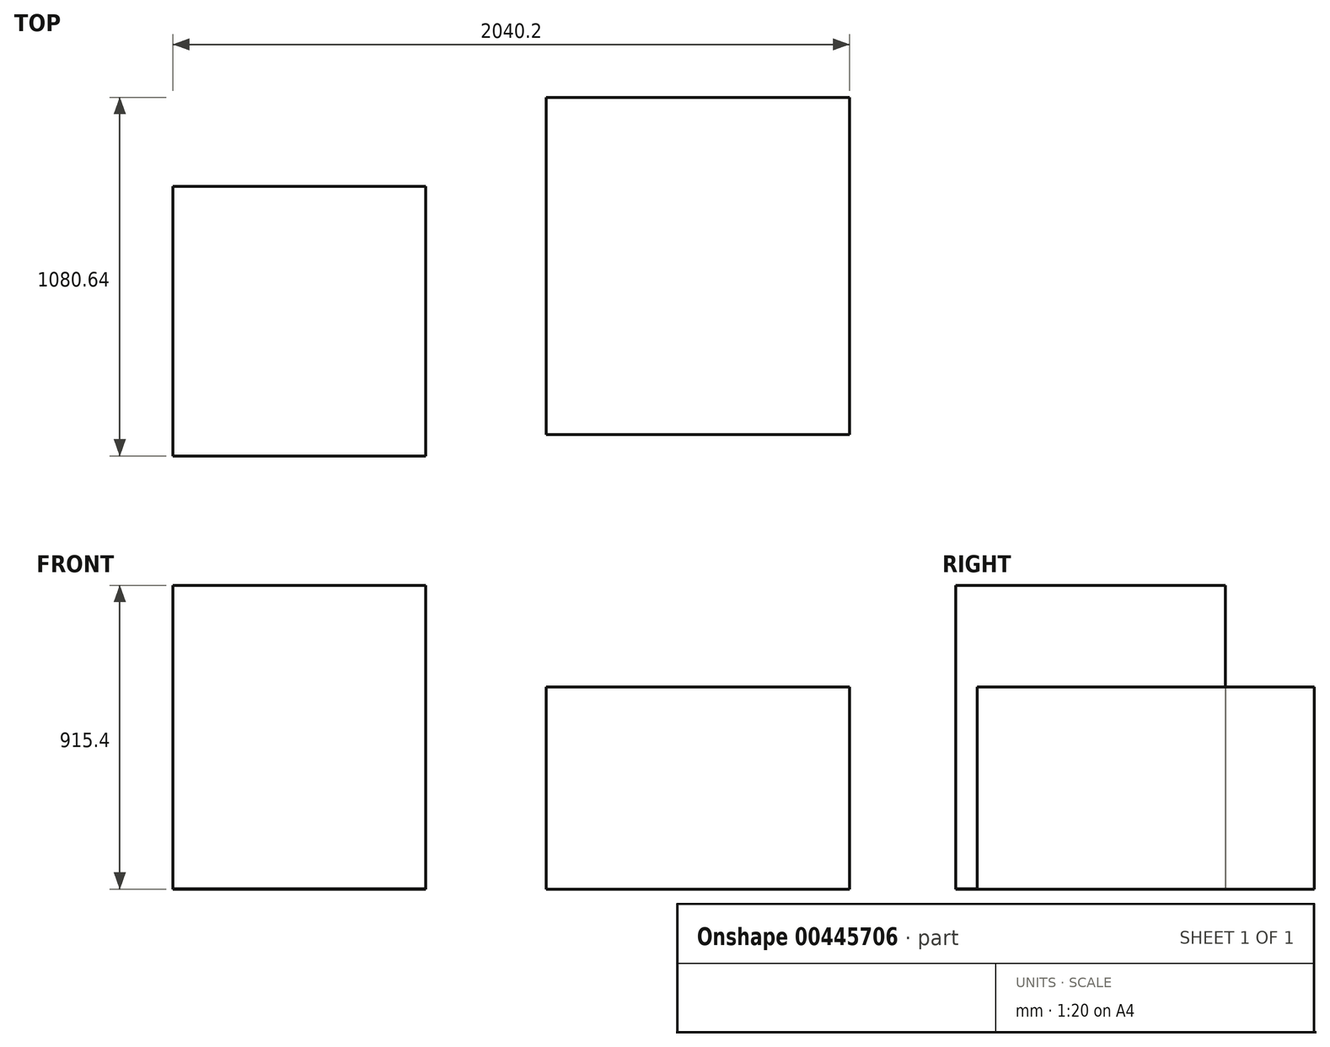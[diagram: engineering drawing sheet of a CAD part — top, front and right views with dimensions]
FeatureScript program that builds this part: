
annotation { "Feature Type Name" : "Feature", "Feature Type Description" : "" }
export const myFeature = defineFeature(function(context is Context, id is Id, definition is map)
    precondition{}
    {
        {
            var Q0;
            Q0=qCreatedBy(makeId("Top.planeOp"),FACE);
            var sketch = newSketch(context, id + "F0", { "sketchPlane" : qUnion([Q0])});
            skLineSegment(sketch, "E0.bottom", {"start": v(-79.69, -64.64) * mm, "end": v(682.31, -64.64) * mm});
            skLineSegment(sketch, "E0.top", {"start": v(-79.69, 748.16) * mm, "end": v(682.31, 748.16) * mm});
            skLineSegment(sketch, "E0.left", {"start": v(-79.69, -64.64) * mm, "end": v(-79.69, 748.16) * mm});
            skLineSegment(sketch, "E0.right", {"start": v(682.31, -64.64) * mm, "end": v(682.31, 748.16) * mm});
            skSolve(sketch);
        }
        {
            var Q0;
            Q0 = qSketchRegion(id + "F0", true);
            extrude(context, id + "F1", {"entities" : qUnion([Q0]), "depth" : 1 * mm});
        }
        {
            var Q0;
            Q0=makeQuery(id+"F1.opExtrude","CAP_FACE",FACE,{"disambiguationData":[OSD([sQuery(id+"F0.wireOp",EDGE,"E0.bottom"),sQuery(id+"F0.wireOp",EDGE,"E0.top"),sQuery(id+"F0.wireOp",EDGE,"E0.left"),sQuery(id+"F0.wireOp",EDGE,"E0.right")])],"isStart":false});
            var sketch = newSketch(context, id + "F2", { "sketchPlane" : qUnion([Q0])});
            skLineSegment(sketch, "E1.bottom", {"start": v(-79.69, -64.64) * mm, "end": v(682.31, -64.64) * mm});
            skLineSegment(sketch, "E1.top", {"start": v(-79.69, 748.16) * mm, "end": v(682.31, 748.16) * mm});
            skLineSegment(sketch, "E1.left", {"start": v(-79.69, -64.64) * mm, "end": v(-79.69, 748.16) * mm});
            skLineSegment(sketch, "E1.right", {"start": v(682.31, -64.64) * mm, "end": v(682.31, 748.16) * mm});
            skSolve(sketch);
        }
        {
            var Q0;
            Q0 = qSketchRegion(id + "F2", true);
            extrude(context, id + "F3", {"entities" : qUnion([Q0]), "depth" : 914.4 * mm});
        }
        {
            var Q0;
            Q0=qCreatedBy(makeId("Top.planeOp"),FACE);
            var sketch = newSketch(context, id + "F4", { "sketchPlane" : qUnion([Q0])});
            skLineSegment(sketch, "E2.bottom", {"start": v(1046.11, 0) * mm, "end": v(1960.51, 0) * mm});
            skLineSegment(sketch, "E2.top", {"start": v(1046.11, 1016) * mm, "end": v(1960.51, 1016) * mm});
            skLineSegment(sketch, "E2.left", {"start": v(1046.11, 0) * mm, "end": v(1046.11, 1016) * mm});
            skLineSegment(sketch, "E2.right", {"start": v(1960.51, 0) * mm, "end": v(1960.51, 1016) * mm});
            skSolve(sketch);
        }
        {
            var Q0;
            Q0 = qSketchRegion(id + "F4", true);
            extrude(context, id + "F5", {"entities" : qUnion([Q0]), "depth" : 609.6 * mm});
        }
    });
